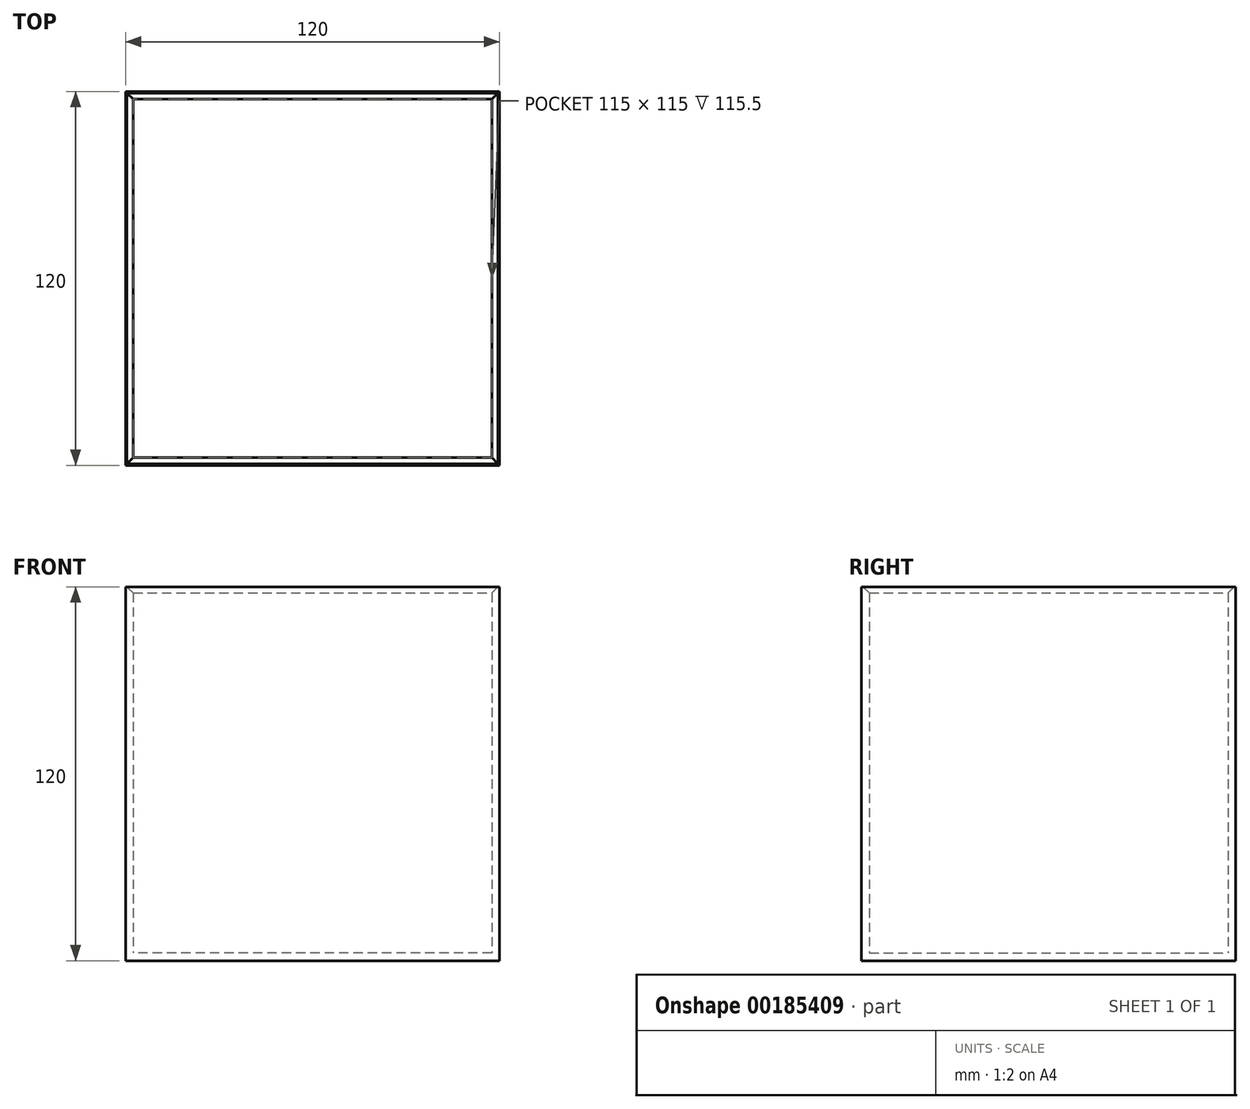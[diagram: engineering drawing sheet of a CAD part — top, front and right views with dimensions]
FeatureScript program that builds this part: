
annotation { "Feature Type Name" : "Feature", "Feature Type Description" : "" }
export const myFeature = defineFeature(function(context is Context, id is Id, definition is map)
    precondition{}
    {
        {
            var Q0;
            Q0=qCreatedBy(makeId("Top.planeOp"),FACE);
            var sketch = newSketch(context, id + "F0", { "sketchPlane" : qUnion([Q0])});
            skLineSegment(sketch, "E0.bottom", {"start": v(60, -60) * mm, "end": v(-60, -60) * mm});
            skLineSegment(sketch, "E0.top", {"start": v(60, 60) * mm, "end": v(-60, 60) * mm});
            skLineSegment(sketch, "E0.left", {"start": v(60, -60) * mm, "end": v(60, 60) * mm});
            skLineSegment(sketch, "E0.right", {"start": v(-60, -60) * mm, "end": v(-60, 60) * mm});
            skPoint(sketch, "E0.middle", {"position": v(0, 0) * mm});
            skSolve(sketch);
        }
        {
            var Q0;
            Q0 = qSketchRegion(id + "F0", true);
            extrude(context, id + "F1", {"entities" : qUnion([Q0]), "depth" : 120 * mm});
        }
        {
            var Q0;
            Q0=makeQuery(id+"F1.opExtrude","CAP_FACE",FACE,{"disambiguationData":[OSD([sQuery(id+"F0.wireOp",EDGE,"E0.bottom"),sQuery(id+"F0.wireOp",EDGE,"E0.top"),sQuery(id+"F0.wireOp",EDGE,"E0.left"),sQuery(id+"F0.wireOp",EDGE,"E0.right")])],"isStart":false});
            shell(context, id + "F2", {"entities" : qUnion([Q0]), "thickness" : 2.5 * mm});
        }
        {
            var Q0;
            {var subQ0=sQuery(id+"F0.wireOp",EDGE,"E0.top");Q0=makeQuery(id+"F2.opShell","OFFSET_EDGE",EDGE,{"disambiguationData":[OSD([subQ0]),TDD([makeQuery(id+"F1.opExtrude","CAP_EDGE",EDGE,{"disambiguationData":[OSD([subQ0])],"isStart":false})])]});}
            var Q1;
            {var subQ0=sQuery(id+"F0.wireOp",EDGE,"E0.right");Q1=makeQuery(id+"F2.opShell","OFFSET_EDGE",EDGE,{"disambiguationData":[OSD([subQ0]),TDD([makeQuery(id+"F1.opExtrude","CAP_EDGE",EDGE,{"disambiguationData":[OSD([subQ0])],"isStart":false})])]});}
            var Q2;
            {var subQ0=sQuery(id+"F0.wireOp",EDGE,"E0.bottom");Q2=makeQuery(id+"F2.opShell","OFFSET_EDGE",EDGE,{"disambiguationData":[OSD([subQ0]),TDD([makeQuery(id+"F1.opExtrude","CAP_EDGE",EDGE,{"disambiguationData":[OSD([subQ0])],"isStart":false})])]});}
            var Q3;
            {var subQ0=sQuery(id+"F0.wireOp",EDGE,"E0.left");Q3=makeQuery(id+"F2.opShell","OFFSET_EDGE",EDGE,{"disambiguationData":[OSD([subQ0]),TDD([makeQuery(id+"F1.opExtrude","CAP_EDGE",EDGE,{"disambiguationData":[OSD([subQ0])],"isStart":false})])]});}
            chamfer(context, id + "F3", {"entities" : qUnion([Q0, Q1, Q2, Q3]), "width" : 2 * mm, "tangentPropagation" : true});
        }
    });
